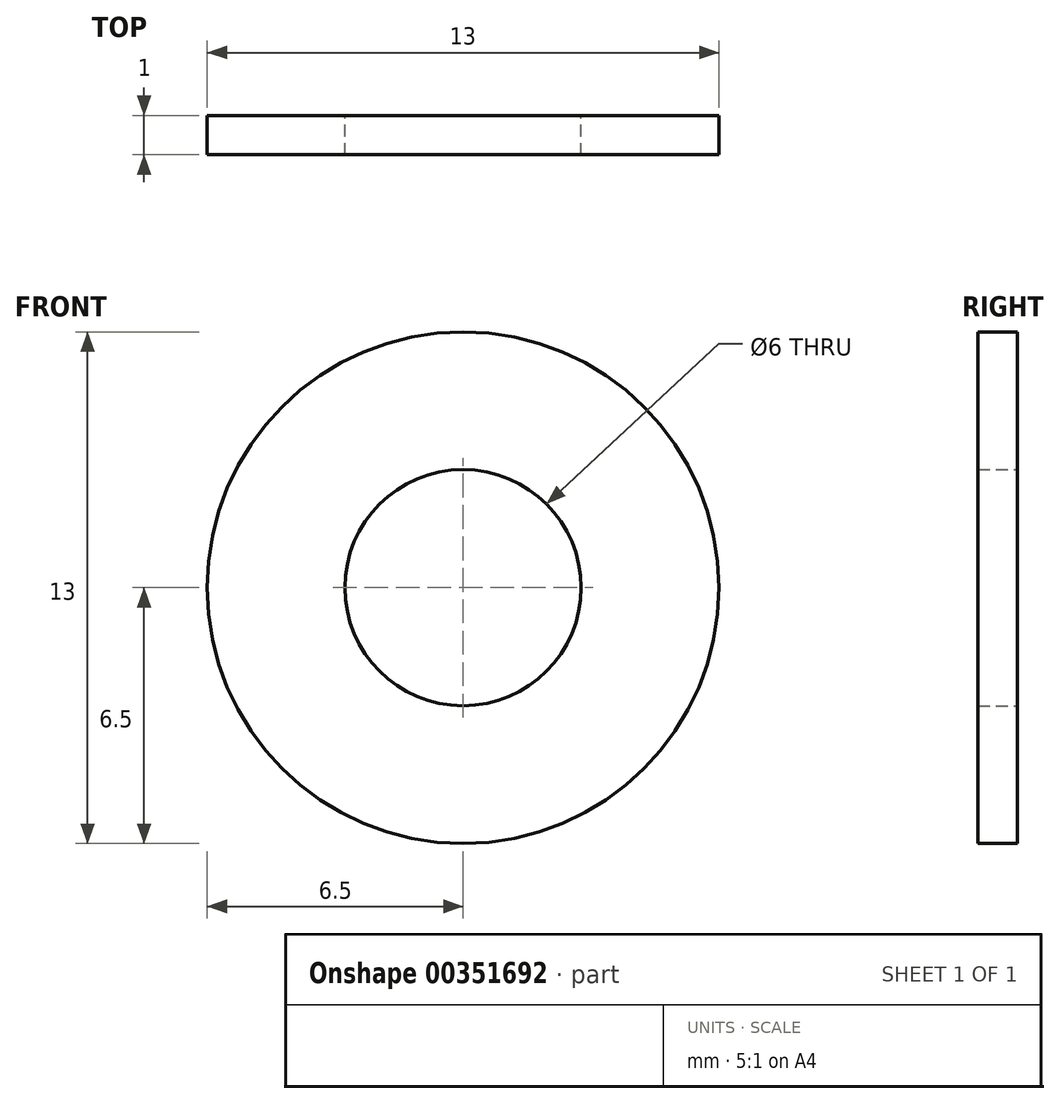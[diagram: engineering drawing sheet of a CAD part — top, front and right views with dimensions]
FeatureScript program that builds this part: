
annotation { "Feature Type Name" : "Feature", "Feature Type Description" : "" }
export const myFeature = defineFeature(function(context is Context, id is Id, definition is map)
    precondition{}
    {
        {
            var Q0;
            Q0=qCreatedBy(makeId("Front.planeOp"),FACE);
            var sketch = newSketch(context, id + "F0", { "sketchPlane" : qUnion([Q0])});
            skCircle(sketch, "E0", {"center": v(0, 0) * mm, "radius": 6.5 * mm});
            skCircle(sketch, "E1", {"center": v(0, 0) * mm, "radius": 3 * mm});
            skSolve(sketch);
        }
        {
            var Q0;
            Q0 = qSketchRegion(id + "F0", true);
            extrude(context, id + "F1", {"entities" : qUnion([Q0]), "endBound" : BoundingType.SYMMETRIC, "depth" : 1 * mm});
        }
    });
